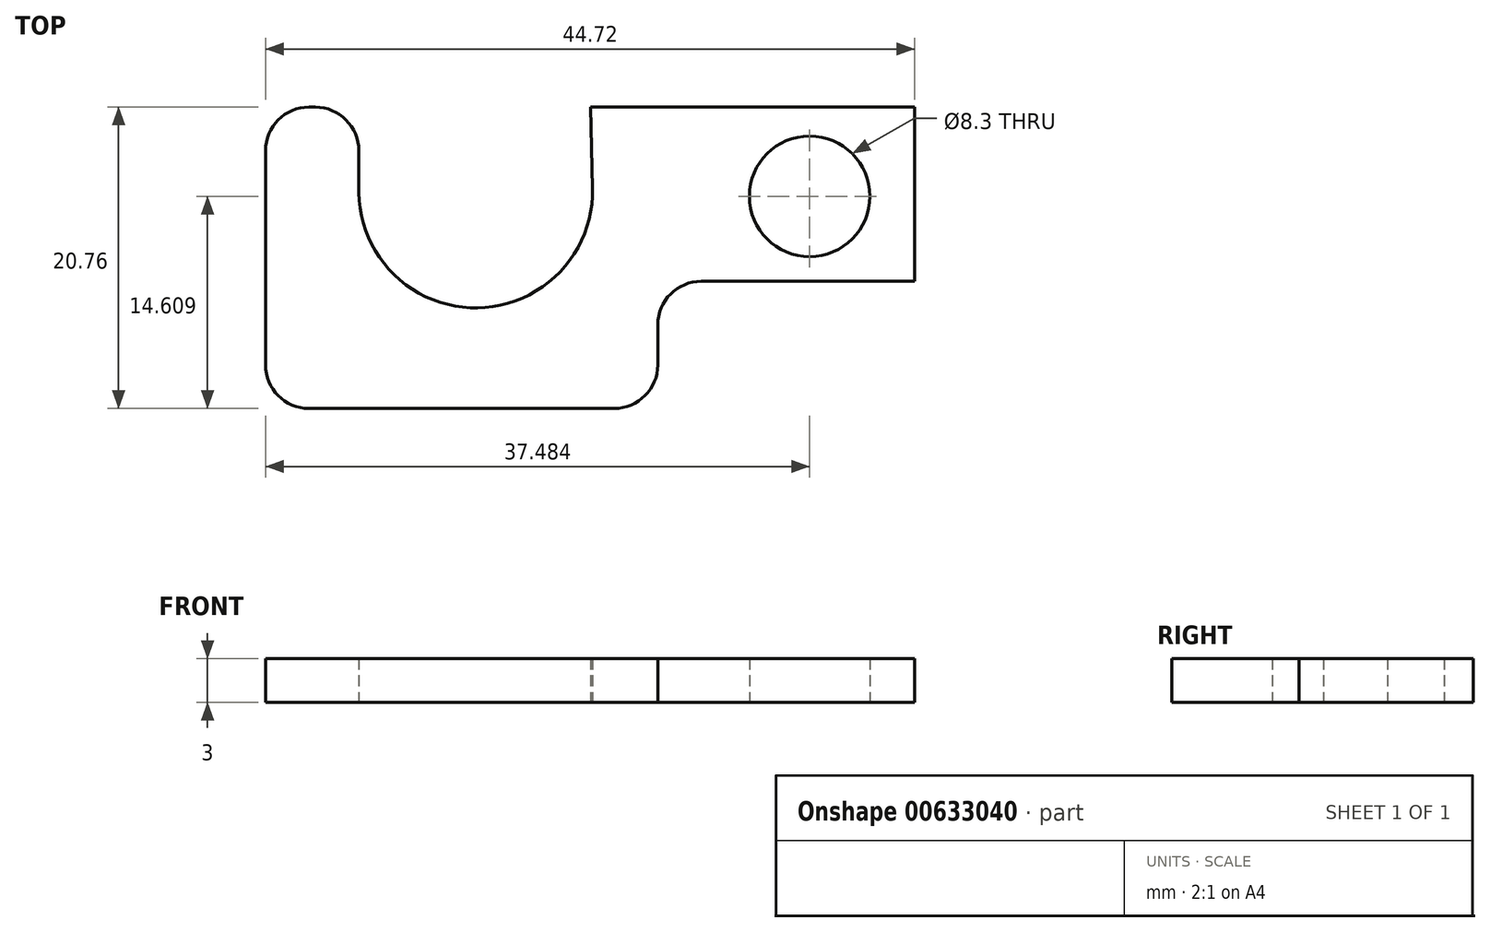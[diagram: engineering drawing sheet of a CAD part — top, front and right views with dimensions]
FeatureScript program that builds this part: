
annotation { "Feature Type Name" : "Feature", "Feature Type Description" : "" }
export const myFeature = defineFeature(function(context is Context, id is Id, definition is map)
    precondition{}
    {
        {
            var Q0;
            Q0=qCreatedBy(makeId("Top.planeOp"),FACE);
            var sketch = newSketch(context, id + "F0", { "sketchPlane" : qUnion([Q0])});
            skLineSegment(sketch, "E0", {"start": v(31.97, 8) * mm, "end": v(9.66, 8) * mm});
            skLineSegment(sketch, "E1", {"start": v(-12.75, 5) * mm, "end": v(-12.75, -9.75) * mm});
            skLineSegment(sketch, "E2", {"start": v(-9.75, -12.75) * mm, "end": v(11.27, -12.75) * mm});
            skLineSegment(sketch, "E3", {"start": v(14.27, -9.75) * mm, "end": v(14.27, -7) * mm});
            skLineSegment(sketch, "E4", {"start": v(17.27, -4) * mm, "end": v(31.97, -4) * mm});
            skLineSegment(sketch, "E5", {"start": v(31.97, -4) * mm, "end": v(31.97, 8) * mm});
            skArc(sketch, "E6", {"start": v(-6.33, 2.34) * mm, "mid": v(1.75, -5.83) * mm, "end": v(9.77, 2.4) * mm});
            skLineSegment(sketch, "E7", {"start": v(-6.33, 2.11) * mm, "end": v(-6.33, 5) * mm});
            skLineSegment(sketch, "E8", {"start": v(9.77, 2.4) * mm, "end": v(9.66, 8) * mm});
            skLineSegment(sketch, "E9.trimOffspring", {"start": v(-9.33, 8) * mm, "end": v(-9.75, 8) * mm});
            skCircle(sketch, "E10", {"center": v(24.73, 1.86) * mm, "radius": 4.15 * mm});
            skPoint(sketch, "E11.visualSharp", {"position": v(14.27, -4) * mm});
            skArc(sketch, "E11.filletArc", {"start": v(17.27, -4) * mm, "mid": v(15.15, -4.87) * mm, "end": v(14.27, -7) * mm});
            skPoint(sketch, "E12.visualSharp", {"position": v(-12.75, -12.75) * mm});
            skArc(sketch, "E12.filletArc", {"start": v(-12.75, -9.75) * mm, "mid": v(-11.88, -11.88) * mm, "end": v(-9.75, -12.75) * mm});
            skPoint(sketch, "E13.visualSharp", {"position": v(14.27, -12.75) * mm});
            skArc(sketch, "E13.filletArc", {"start": v(11.27, -12.75) * mm, "mid": v(13.4, -11.88) * mm, "end": v(14.27, -9.75) * mm});
            skPoint(sketch, "E14.visualSharp", {"position": v(-12.75, 8) * mm});
            skArc(sketch, "E14.filletArc", {"start": v(-9.75, 8) * mm, "mid": v(-11.88, 7.13) * mm, "end": v(-12.75, 5) * mm});
            skPoint(sketch, "E15.visualSharp", {"position": v(-6.33, 8) * mm});
            skArc(sketch, "E15.filletArc", {"start": v(-6.33, 5) * mm, "mid": v(-7.2, 7.13) * mm, "end": v(-9.33, 8) * mm});
            skSolve(sketch);
        }
        {
            var Q0;
            Q0=qSketchRegion(id+"F0",true);
            extrude(context, id + "F1", {"entities" : qUnion([Q0]), "depth" : 3 * mm});
        }
    });
